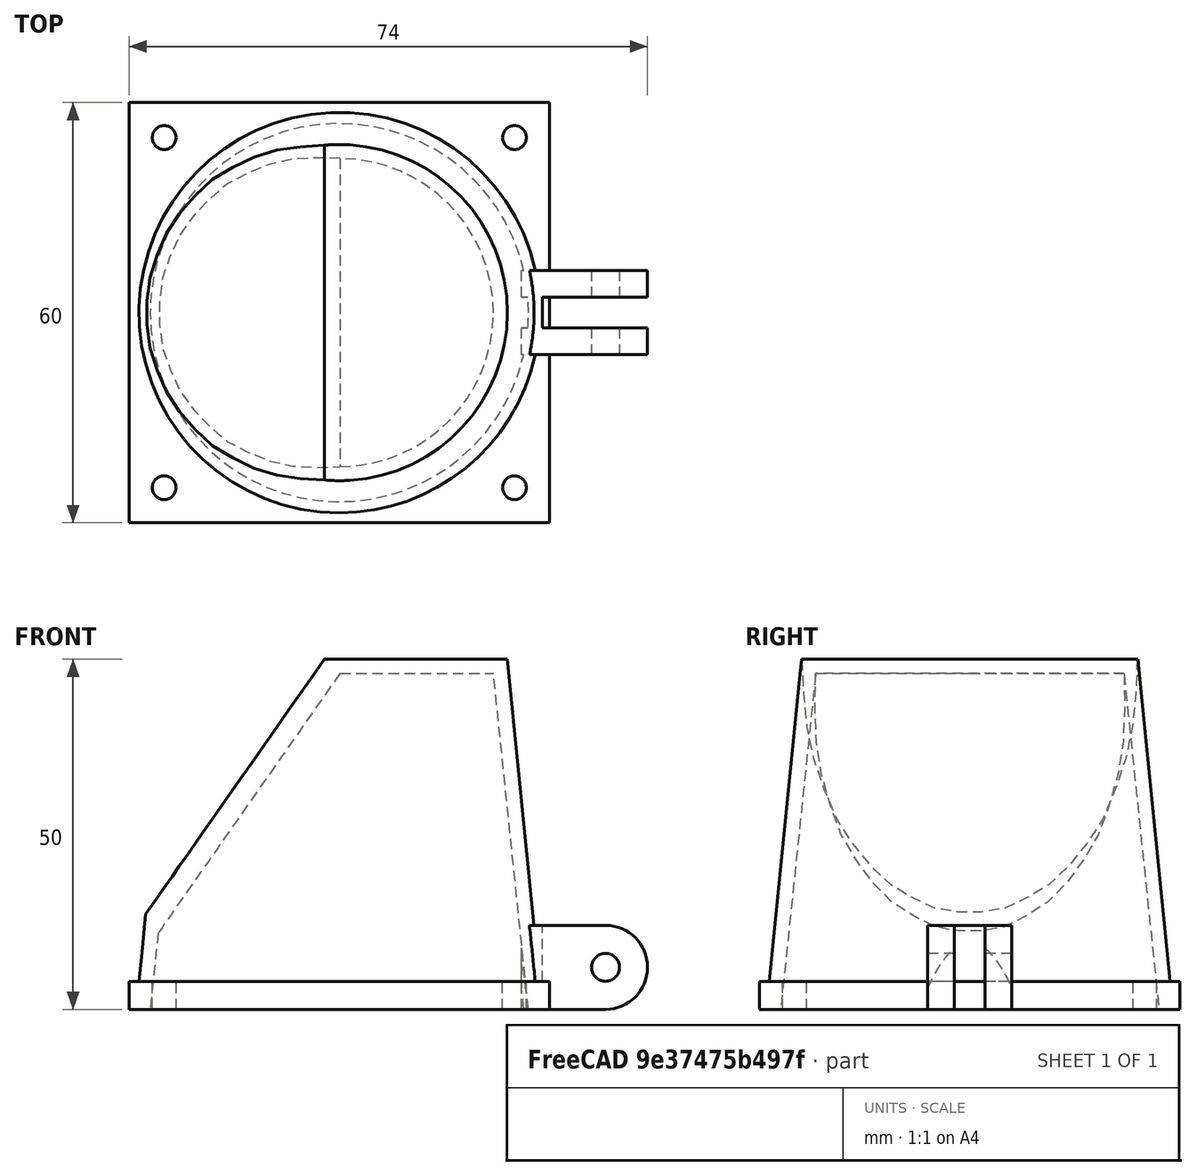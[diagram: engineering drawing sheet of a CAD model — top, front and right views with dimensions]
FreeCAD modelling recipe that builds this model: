
FCSTD DOCUMENT
Label: Fan_duct_3
objects: Part::Cut×8, Part::Cylinder×6, Part::Fuse×6, Part::Box×5, Part::Cone×3, Mesh::Feature×1, Part::Common×1
note: 29 computed .brp shape members not serialized (recipe doc carries the construction recipe); baked Part::Feature solids carry a one-line shape summary decoded from their .brp

FEATURE [Mesh::Feature] fan_mount_fan
  Placement = pos=(-47,21,0) rot=(0,0,1;0rad)
FEATURE [Part::Box] Box
  Height = 4
  Length = 60
  Width = 60
FEATURE [Part::Cylinder] Cylinder
  Angle = 360
  Height = 10
  Placement = pos=(5,5,-4) rot=(0,0,1;0rad)
  Radius = 1.7
FEATURE [Part::Cylinder] Cylinder001
  Angle = 360
  Height = 10
  Placement = pos=(55,5,-4) rot=(0,0,1;0rad)
  Radius = 1.7
FEATURE [Part::Cylinder] Cylinder002
  Angle = 360
  Height = 10
  Placement = pos=(5,55,-4) rot=(0,0,1;0rad)
  Radius = 1.7
FEATURE [Part::Cylinder] Cylinder002001
  Angle = 360
  Height = 10
  Placement = pos=(55,55,-4) rot=(0,0,1;0rad)
  Radius = 1.7
FEATURE [Part::Cut] Cut
  Base = -> Box
  Tool = -> Cylinder
FEATURE [Part::Cut] Cut001
  Base = -> Cut
  Tool = -> Cylinder001
FEATURE [Part::Cut] Cut002
  Base = -> Cut001
  Tool = -> Cylinder002
FEATURE [Part::Cut] Cut003  label="Base1"
  Base = -> Cut002
  Tool = -> Cylinder002001
FEATURE [Part::Cone] Cone  label="Corps du duct"
  Angle = 360
  Height = 50
  Placement = pos=(30,30,0) rot=(0,0,1;0rad)
  Radius1 = 29
  Radius2 = 24
FEATURE [Part::Cone] Cone001  label="Trou principal"
  Angle = 360
  Height = 48
  Placement = pos=(30,30,0) rot=(0,0,1;0rad)
  Radius1 = 27
  Radius2 = 22
FEATURE [Part::Box] Box001
  Height = 3
  Length = 60
  Placement = pos=(0,0,5) rot=(0,-1,0;0.959932rad)
  Width = 60
FEATURE [Part::Cone] Cone002
  Angle = 360
  Height = 50
  Placement = pos=(30,30,0) rot=(0,0,1;0rad)
  Radius1 = 29
  Radius2 = 24
FEATURE [Part::Common] Common  label="Meplat"
  Base = -> Box001
  Tool = -> Cone002
FEATURE [Part::Box] Box001001  label="A retirer pour meplat"
  Height = 24
  Length = 60
  Placement = pos=(0,0,5) rot=(0,-1,0;0.959932rad)
  Width = 60
FEATURE [Part::Fuse] Fusion  label="Base2"
  Base = -> Cut003
  Tool = -> Cone
FEATURE [Part::Cut] Cut004  label="Base3"
  Base = -> Fusion
  Tool = -> Cone001
FEATURE [Part::Cut] Cut005  label="Base4"
  Base = -> Cut004
  Tool = -> Box001001
FEATURE [Part::Fuse] Fusion001  label="Base5"
  Base = -> Cut005
  Tool = -> Common
FEATURE [Part::Cylinder] Cylinder002002
  Angle = 360
  Height = 3.8
  Placement = pos=(68,27.8,6) rot=(1,0,0;1.5708rad)
  Radius = 6
FEATURE [Part::Cylinder] Cylinder002002001
  Angle = 360
  Height = 4.8
  Placement = pos=(68,28,6) rot=(1,0,0;1.5708rad)
  Radius = 2
FEATURE [Part::Box] Box001003  label="Plat languettes"
  Height = 12
  Length = 2
  Placement = pos=(57,24,0) rot=(0,0,1;0rad)
  Width = 12
FEATURE [Part::Box] Box001004
  Height = 12
  Length = 12
  Placement = pos=(56,24,0) rot=(0,0,1;0rad)
  Width = 3.8
FEATURE [Part::Fuse] Fusion002
  Base = -> Box001004
  Tool = -> Cylinder002002
FEATURE [Part::Cut] Cut006  label="Languette1"
  Base = -> Fusion002
  Tool = -> Cylinder002002001
FEATURE [Part::Cut] Cut006001  label="Languette002"
  Base = -> Fusion002
  Placement = pos=(0,8.2,0) rot=(0,0,1;0rad)
  Tool = -> Cylinder002002001
FEATURE [Part::Fuse] Fusion003
  Base = -> Box001003
  Tool = -> Cut006
FEATURE [Part::Fuse] Fusion004  label="Languette tot"
  Base = -> Fusion003
  Tool = -> Cut006001
FEATURE [Part::Fuse] Fusion005  label="Fan duct 3"
  Base = -> Fusion001
  Tool = -> Fusion004
